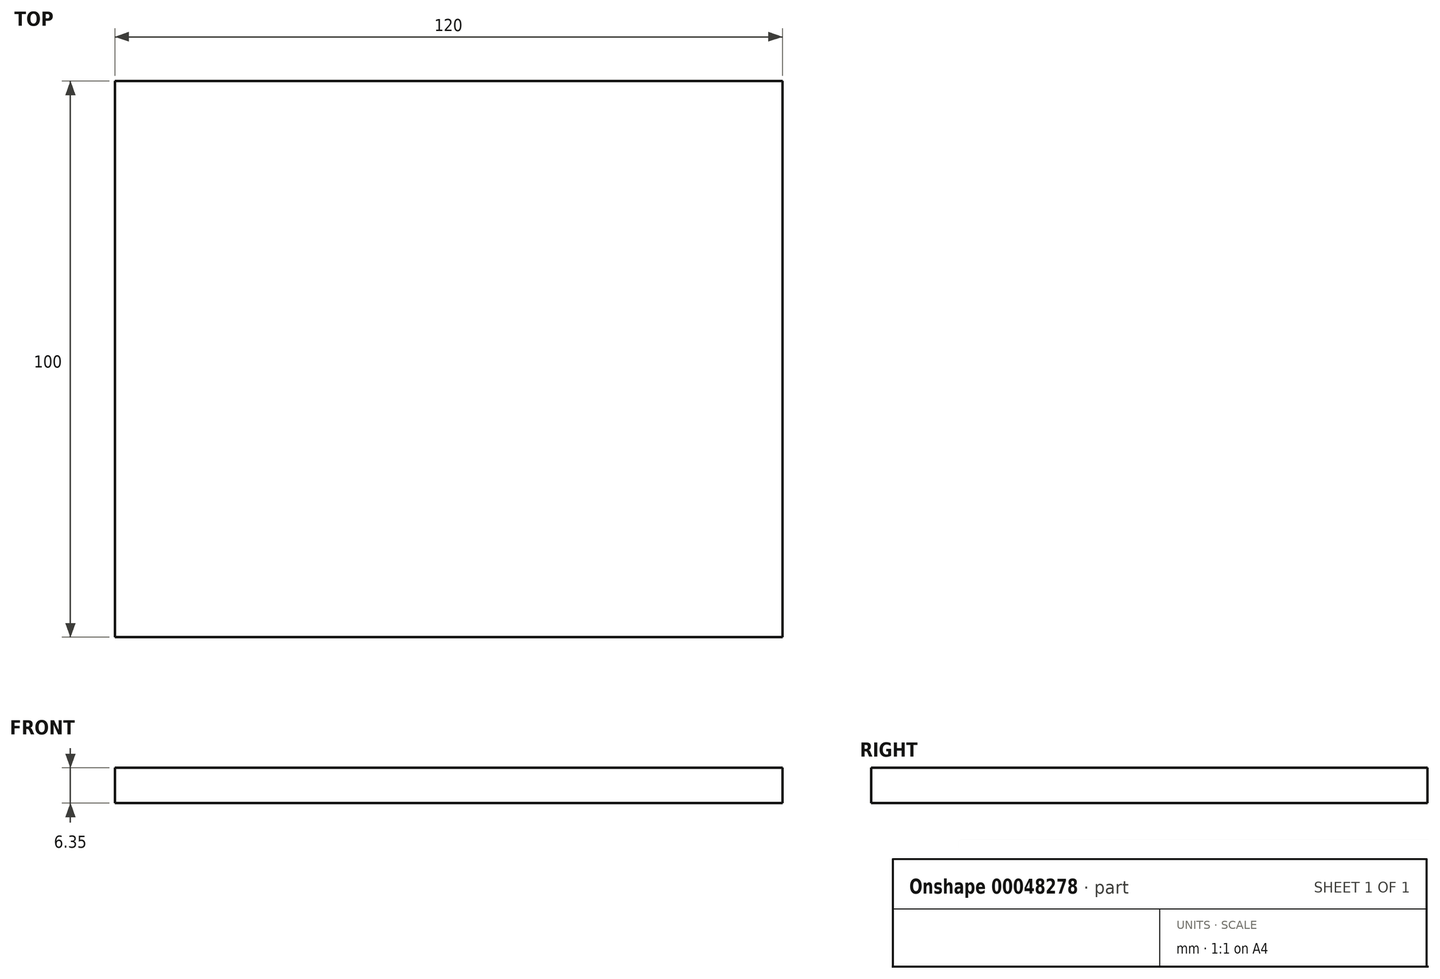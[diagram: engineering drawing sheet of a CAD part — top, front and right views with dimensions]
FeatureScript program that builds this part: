
annotation { "Feature Type Name" : "Feature", "Feature Type Description" : "" }
export const myFeature = defineFeature(function(context is Context, id is Id, definition is map)
    precondition{}
    {
        {
            var Q0;
            Q0=qCreatedBy(makeId("Top.planeOp"),FACE);
            var sketch = newSketch(context, id + "F0", { "sketchPlane" : qUnion([Q0])});
            skLineSegment(sketch, "E0", {"start": v(-60, 50) * mm, "end": v(-60, -50) * mm});
            skLineSegment(sketch, "E1", {"start": v(-60, -50) * mm, "end": v(60, -50) * mm});
            skLineSegment(sketch, "E2", {"start": v(60, -50) * mm, "end": v(60, 50) * mm});
            skLineSegment(sketch, "E3", {"start": v(60, 50) * mm, "end": v(-60, 50) * mm});
            skSolve(sketch);
        }
        {
            var Q0;
            Q0 = qSketchRegion(id + "F0", true);
            extrude(context, id + "F1", {"entities" : qUnion([Q0]), "depth" : 6.35 * mm});
        }
    });
